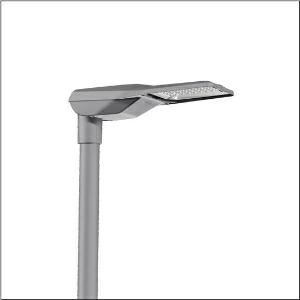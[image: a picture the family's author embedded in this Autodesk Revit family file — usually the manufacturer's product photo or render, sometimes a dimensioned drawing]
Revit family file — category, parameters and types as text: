
# Revit family: streetlight_sl_21_iq_mini___st0_5a_5xe2b41d08hb_2494
name_source: partatom
category: Lighting Fixtures
units: mm (PartAtom-declared; Revit-internal decimal feet)

## family parameters
Cut with Voids When Loaded = No
Host = Face
Light Source = No
Part Type = Normal
Room Calculation Point = No
Round Connector Dimension = Use Diameter
Shared = No

## types (1)
- --- (1 x LED, 9860 lm, 70.9 W, 4000K)
    Apparent Load = 71 VA
    CIE Flux Codes = 41 75 97 100 100
    Color Rendering = 70
    Color Temperature = 4000K
    Default Elevation = 1800 mm
    Description = Streetlight SL 21 iQ mini, mast luminaire, primary light control with lens, of PMMA, primary optical cover: cover, of toughened safety glass, transparent, light distribution: ST0.5a, light emission: direct distribution, primary light characteristic: asymmetric, installation type: post-top, side-entry, LED, High Power LED, rated luminous flux: 9.860lm, luminous efficacy: 139lm/W, light colour: 740, colour temperature: 4000K, control: Auto-Match, Temp-Guard, Lumen-Switch, Night-Set, Smart-Wire, Light-Fading, Desk-Remote (wireless, voltage-free reading and setting of iQ features in the workshop via application-optimized NFC function/RFID function), optimised constant luminous flux control (CLO 2.0), presetting dimming linear, mains connection: 220..240V, AC, 50/60Hz, start of lifetime: 71W, end of service life: 75W, reduction: 31W, luminaire housing, of diecast aluminium, powder-coated, Siteco® metallic grey (DB 702S), corrosivity category C5 mid according to DIN EN ISO 12944, please order mast flange separately, inclination adjustable: 0°, 5°, 10°, 15°, sealing non-destructively replaceable, multi-level sealing system, length: 628mm, width: 235mm, height: 110mm, mast flange for spigot size: 42mm (side-entry): 5XC10008XM4, 60/48mm (side-entry/post-top): 5XC10108XM2, 76/60mm (side-entry/post-top): 5XC10108XM1, protection rating (complete): IP66, insulation class (complete): insulation class II (safety insulation), certification: CE, ENEC, ENEC+, VDE, impact resistance: IK09, permissible operating ambient temperature for outdoor applications: -40..+50°C, standard-compliant lighting for roads and squares, packaging unit: 1 piece

Light Distribution: ST0.5a
    Height = 110 mm
    Lamp = 1 x LED
    Lamp Light Flux = 9860 lm
    Lamp Power = 70.9 W
    Lamp count = 1
    Length = 625 mm
    Luminous efficacy = 139 lm/W
    Manufacturer = Siteco
    ModVariant = No
    Model = 5XE2B41D08HB
    Number of Poles = 1
    OnlyDefault = Yes
    Power Factor = 1
    Product Name = Streetlight SL 21 iQ mini | ST0.5a
    Product group = mast luminaire | pylon top
    ProductGroupID = 6100
    Protection Class = Protection class II
    Protection Degree = IP 66
    RLX_Detail_Level = 1
    RLX_Emergency_Light_Flux = 0 lm
    RLX_Emergency_Type = 0
    RLX_Emergency_Type_DB = No
    RlxData = <blob elided: 103597 chars, md5=18ea9263>
    Socket = socket
    Standby Power = 0 W
    System Light Flux = 9860 lm
    System Power = 71 W
    Type Comments = factory setting: luminous flux: 100 % | dim-lin: 254 | 711 mA
    Type Image = l_1003519.jpg
    URL = http://relux.com
    VarID = @adj_090875
    Voltage = 0 V
    Weight = 0.00 kg
    Width = 234 mm

## geometry (parser evidence)
native form markers: Blend x4, Sweep x11
no freeform markers — native parametric forms only
